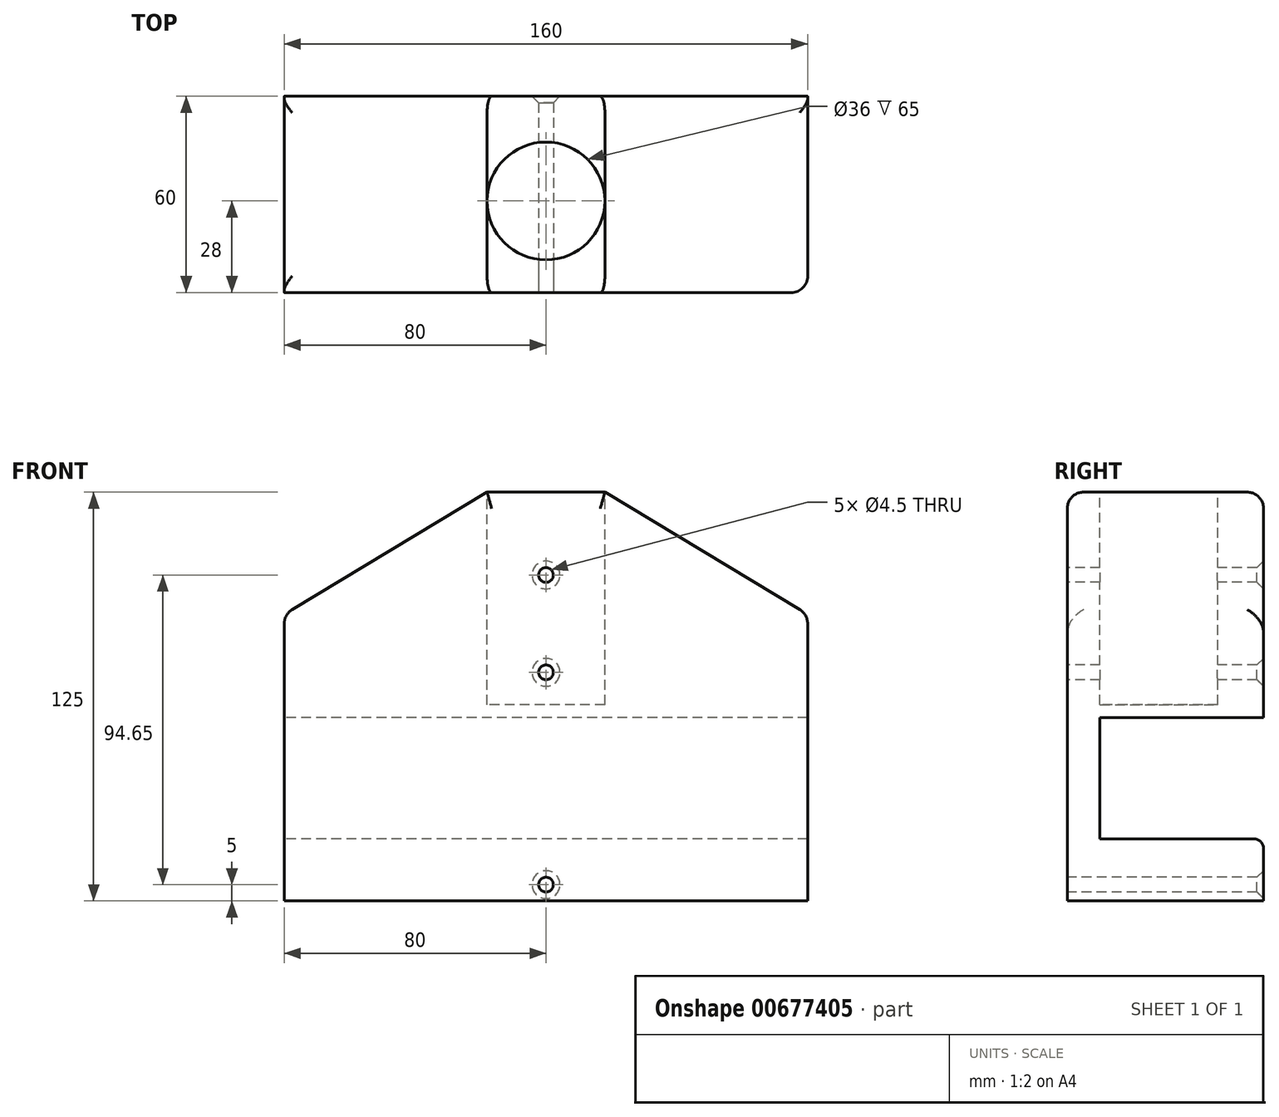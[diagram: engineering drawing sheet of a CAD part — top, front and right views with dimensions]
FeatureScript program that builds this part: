
annotation { "Feature Type Name" : "Feature", "Feature Type Description" : "" }
export const myFeature = defineFeature(function(context is Context, id is Id, definition is map)
    precondition{}
    {
        {
            var Q0;
            Q0=qCreatedBy(makeId("Front.planeOp"),FACE);
            var sketch = newSketch(context, id + "F0", { "sketchPlane" : qUnion([Q0])});
            skLineSegment(sketch, "E0.bottom", {"start": v(-80, 0) * mm, "end": v(80, 0) * mm});
            skLineSegment(sketch, "E0.top", {"start": v(-18, 125) * mm, "end": v(18, 125) * mm});
            skLineSegment(sketch, "E0.left", {"start": v(-80, 0) * mm, "end": v(-80, 87.62) * mm});
            skLineSegment(sketch, "E0.right", {"start": v(80, 0) * mm, "end": v(80, 87.62) * mm});
            skLineSegment(sketch, "E1", {"start": v(80, 87.62) * mm, "end": v(18, 125) * mm});
            skLineSegment(sketch, "E2", {"start": v(-80, 87.62) * mm, "end": v(-18, 125) * mm});
            skSolve(sketch);
        }
        {
            var Q0;
            Q0 = qSketchRegion(id + "F0", true);
            extrude(context, id + "F1", {"entities" : qUnion([Q0]), "oppositeDirection" : true, "depth" : 60 * mm, "offsetDistance" : 25 * mm});
        }
        {
            var Q0;
            Q0=makeQuery(id+"F1.opExtrude","SWEPT_FACE",FACE,{"disambiguationData":[OSD([sQuery(id+"F0.wireOp",EDGE,"E0.top")])]});
            var sketch = newSketch(context, id + "F2", { "sketchPlane" : qUnion([Q0])});
            skCircle(sketch, "E3", {"center": v(0, 28) * mm, "radius": 18 * mm});
            skPoint(sketch, "E3.centerSnap0", {"position": v(0, 0) * mm});
            skSolve(sketch);
        }
        {
            var Q0;
            Q0=makeQuery(id+"F1.opExtrude","SWEPT_FACE",FACE,{"disambiguationData":[OSD([sQuery(id+"F0.wireOp",EDGE,"E0.left")])]});
            var sketch = newSketch(context, id + "F3", { "sketchPlane" : qUnion([Q0])});
            skLineSegment(sketch, "E4.bottom", {"start": v(-60, 56) * mm, "end": v(-10, 56) * mm});
            skLineSegment(sketch, "E4.top", {"start": v(-60, 19) * mm, "end": v(-10, 19) * mm});
            skLineSegment(sketch, "E4.left", {"start": v(-60, 56) * mm, "end": v(-60, 19) * mm});
            skLineSegment(sketch, "E4.right", {"start": v(-10, 56) * mm, "end": v(-10, 19) * mm});
            skSolve(sketch);
        }
        {
            var Q0;
            Q0 = qSketchRegion(id + "F3", true);
            extrude(context, id + "F4", {"entities" : qUnion([Q0]), "operationType" : NewBodyOperationType.REMOVE, "endBound" : BoundingType.UP_TO_NEXT, "oppositeDirection" : true, "depth" : 25 * mm, "offsetDistance" : 25 * mm});
        }
        {
            var Q0;
            {var subQ0=sQuery(id+"F2.wireOp",EDGE,"E3");var subQ1=sQuery(id+"F0.wireOp",EDGE,"E0.top");var subQ2=makeQuery(id+"F2.imprint","INTERSECT",VERTEX,{"derivedFrom":[makeQuery(id+"F1.opExtrude","SWEPT_EDGE",EDGE,{"disambiguationData":[OSD([subQ1,sQuery(id+"F0.wireOp",EDGE,"E2")])]}),subQ0]});Q0=makeQuery(id+"F2.imprint","IMPRINT",FACE,{"disambiguationData":[TD([[makeQuery(id+"F2.imprint","IMPRINT",EDGE,{"disambiguationData":[TD([[subQ2,1.0]])],"derivedFrom":subQ0}),1.0]])]});}
            extrude(context, id + "F5", {"entities" : qUnion([Q0]), "operationType" : NewBodyOperationType.REMOVE, "oppositeDirection" : true, "depth" : 65 * mm, "offsetDistance" : 25 * mm});
        }
        {
            var Q0;
            Q0=makeQuery(id+"F4.boolean.opBoolean","COPY",EDGE,{"derivedFrom":makeQuery(id+"F4.opExtrude","SWEPT_EDGE",EDGE,{"disambiguationData":[OSD([sQuery(id+"F0.wireOp",EDGE,"E0.left"),sQuery(id+"F3.wireOp",EDGE,"E4.bottom"),sQuery(id+"F3.wireOp",EDGE,"E4.left")])]})});
            var Q1;
            Q1=makeQuery(id+"F4.boolean.opBoolean","COPY",EDGE,{"derivedFrom":makeQuery(id+"F4.opExtrude","SWEPT_EDGE",EDGE,{"disambiguationData":[OSD([sQuery(id+"F0.wireOp",EDGE,"E0.left"),sQuery(id+"F3.wireOp",EDGE,"E4.top"),sQuery(id+"F3.wireOp",EDGE,"E4.left")])]})});
            fillet(context, id + "F6", {"entities" : qUnion([Q0, Q1]), "radius" : 3 * mm, "tangentPropagation" : true, "allowEdgeOverflow" : false});
        }
        {
            var Q0;
            Q0=makeQuery(id+"F1.opExtrude","CAP_EDGE",EDGE,{"disambiguationData":[OSD([sQuery(id+"F0.wireOp",EDGE,"E0.top")])],"isStart":false});
            var Q1;
            Q1=makeQuery(id+"F1.opExtrude","CAP_EDGE",EDGE,{"disambiguationData":[OSD([sQuery(id+"F0.wireOp",EDGE,"E2")])],"isStart":false});
            var Q2;
            Q2=makeQuery(id+"F1.opExtrude","CAP_EDGE",EDGE,{"disambiguationData":[OSD([sQuery(id+"F0.wireOp",EDGE,"E1")])],"isStart":false});
            var Q3;
            Q3=makeQuery(id+"F1.opExtrude","SWEPT_EDGE",EDGE,{"disambiguationData":[OSD([sQuery(id+"F0.wireOp",EDGE,"E0.left"),sQuery(id+"F0.wireOp",EDGE,"E2")])]});
            var Q4;
            Q4=makeQuery(id+"F1.opExtrude","CAP_EDGE",EDGE,{"disambiguationData":[OSD([sQuery(id+"F0.wireOp",EDGE,"E2")])],"isStart":true});
            var Q5;
            Q5=makeQuery(id+"F1.opExtrude","CAP_EDGE",EDGE,{"disambiguationData":[OSD([sQuery(id+"F0.wireOp",EDGE,"E1")])],"isStart":true});
            var Q6;
            Q6=makeQuery(id+"F1.opExtrude","SWEPT_EDGE",EDGE,{"disambiguationData":[OSD([sQuery(id+"F0.wireOp",EDGE,"E0.right"),sQuery(id+"F0.wireOp",EDGE,"E1")])]});
            var Q7;
            Q7=makeQuery(id+"F1.opExtrude","CAP_EDGE",EDGE,{"disambiguationData":[OSD([sQuery(id+"F0.wireOp",EDGE,"E0.top")])],"isStart":true});
            var Q8;
            Q8=makeQuery(id+"F1.opExtrude","CAP_EDGE",EDGE,{"disambiguationData":[OSD([sQuery(id+"F0.wireOp",EDGE,"E0.right")])],"isStart":true});
            fillet(context, id + "F7", {"entities" : qUnion([Q0, Q1, Q2, Q3, Q4, Q5, Q6, Q7, Q8]), "radius" : 5 * mm, "tangentPropagation" : true, "allowEdgeOverflow" : false});
        }
        {
            var Q0;
            Q0=makeQuery(id+"F1.opExtrude","CAP_FACE",FACE,{"disambiguationData":[OSD([sQuery(id+"F0.wireOp",EDGE,"E0.bottom"),sQuery(id+"F0.wireOp",EDGE,"E0.top"),sQuery(id+"F0.wireOp",EDGE,"E0.left"),sQuery(id+"F0.wireOp",EDGE,"E0.right"),sQuery(id+"F0.wireOp",EDGE,"E1"),sQuery(id+"F0.wireOp",EDGE,"E2")])],"isStart":true});
            var sketch = newSketch(context, id + "F8", { "sketchPlane" : qUnion([Q0])});
            skCircle(sketch, "E5", {"center": v(0, 99.65) * mm, "radius": 2.25 * mm});
            skCircle(sketch, "E6", {"center": v(0, 69.9) * mm, "radius": 2.25 * mm});
            skCircle(sketch, "E7", {"center": v(0, 5) * mm, "radius": 2.25 * mm});
            skSolve(sketch);
        }
        {
            var Q0;
            Q0 = qSketchRegion(id + "F8", true);
            extrude(context, id + "F9", {"entities" : qUnion([Q0]), "operationType" : NewBodyOperationType.REMOVE, "endBound" : BoundingType.THROUGH_ALL, "oppositeDirection" : true, "depth" : 25 * mm, "offsetDistance" : 25 * mm});
        }
        {
            var Q0;
            {var subQ0=sQuery(id+"F0.wireOp",EDGE,"E1");var subQ1=sQuery(id+"F0.wireOp",EDGE,"E0.right");var subQ2=sQuery(id+"F0.wireOp",EDGE,"E0.left");var subQ3=sQuery(id+"F0.wireOp",EDGE,"E0.top");var subQ4=sQuery(id+"F0.wireOp",EDGE,"E2");Q0=makeQuery(id+"F9.boolean.opBoolean","INTERSECT",EDGE,{"derivedFrom":[makeQuery(id+"F4.boolean.opBoolean","SPLIT",FACE,{"disambiguationData":[TD([makeQuery(id+"F1.opExtrude","SWEPT_FACE",FACE,{"disambiguationData":[OSD([subQ3])]})])],"derivedFrom":makeQuery(id+"F1.opExtrude","CAP_FACE",FACE,{"disambiguationData":[OSD([sQuery(id+"F0.wireOp",EDGE,"E0.bottom"),subQ3,subQ2,subQ1,subQ0,subQ4])],"isStart":false})}),makeQuery(id+"F9.opExtrude","SWEPT_FACE",FACE,{"disambiguationData":[OSD([sQuery(id+"F8.wireOp",EDGE,"E5")])]})]});}
            var Q1;
            {var subQ0=sQuery(id+"F0.wireOp",EDGE,"E1");var subQ1=sQuery(id+"F0.wireOp",EDGE,"E0.right");var subQ2=sQuery(id+"F0.wireOp",EDGE,"E0.left");var subQ3=sQuery(id+"F0.wireOp",EDGE,"E0.top");var subQ4=sQuery(id+"F0.wireOp",EDGE,"E2");Q1=makeQuery(id+"F9.boolean.opBoolean","INTERSECT",EDGE,{"derivedFrom":[makeQuery(id+"F4.boolean.opBoolean","SPLIT",FACE,{"disambiguationData":[TD([makeQuery(id+"F1.opExtrude","SWEPT_FACE",FACE,{"disambiguationData":[OSD([subQ3])]})])],"derivedFrom":makeQuery(id+"F1.opExtrude","CAP_FACE",FACE,{"disambiguationData":[OSD([sQuery(id+"F0.wireOp",EDGE,"E0.bottom"),subQ3,subQ2,subQ1,subQ0,subQ4])],"isStart":false})}),makeQuery(id+"F9.opExtrude","SWEPT_FACE",FACE,{"disambiguationData":[OSD([sQuery(id+"F8.wireOp",EDGE,"E6")])]})]});}
            var Q2;
            {var subQ0=sQuery(id+"F0.wireOp",EDGE,"E0.bottom");var subQ1=sQuery(id+"F0.wireOp",EDGE,"E0.right");var subQ2=sQuery(id+"F0.wireOp",EDGE,"E0.left");Q2=makeQuery(id+"F9.boolean.opBoolean","INTERSECT",EDGE,{"derivedFrom":[makeQuery(id+"F4.boolean.opBoolean","SPLIT",FACE,{"disambiguationData":[TD([makeQuery(id+"F1.opExtrude","SWEPT_FACE",FACE,{"disambiguationData":[OSD([subQ0])]})])],"derivedFrom":makeQuery(id+"F1.opExtrude","CAP_FACE",FACE,{"disambiguationData":[OSD([subQ0,sQuery(id+"F0.wireOp",EDGE,"E0.top"),subQ2,subQ1,sQuery(id+"F0.wireOp",EDGE,"E1"),sQuery(id+"F0.wireOp",EDGE,"E2")])],"isStart":false})}),makeQuery(id+"F9.opExtrude","SWEPT_FACE",FACE,{"disambiguationData":[OSD([sQuery(id+"F8.wireOp",EDGE,"E7")])]})]});}
            chamfer(context, id + "F10", {"entities" : qUnion([Q0, Q1, Q2]), "width" : 2 * mm, "tangentPropagation" : true});
        }
    });
